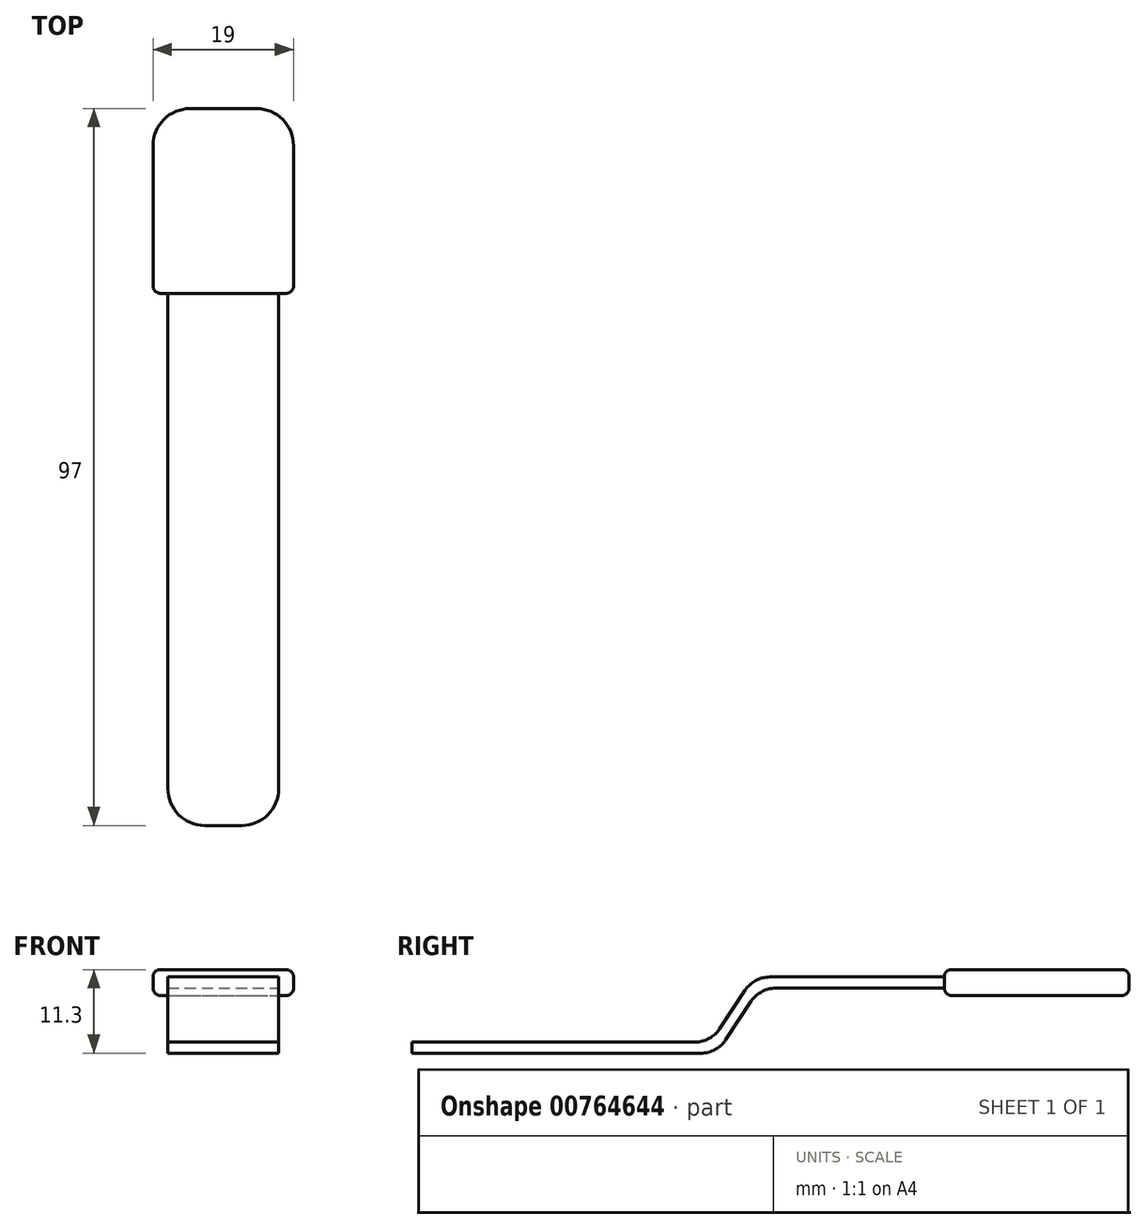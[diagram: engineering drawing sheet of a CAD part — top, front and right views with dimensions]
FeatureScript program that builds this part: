
annotation { "Feature Type Name" : "Feature", "Feature Type Description" : "" }
export const myFeature = defineFeature(function(context is Context, id is Id, definition is map)
    precondition{}
    {
        {
            var Q0;
            Q0=qCreatedBy(makeId("Right.planeOp"),FACE);
            var sketch = newSketch(context, id + "F0", { "sketchPlane" : qUnion([Q0])});
            skLineSegment(sketch, "E0.bottom", {"start": v(-8.38, 4.9) * mm, "end": v(15.22, 4.9) * mm});
            skLineSegment(sketch, "E0.top", {"start": v(-56.78, -5.4) * mm, "end": v(-17.68, -5.4) * mm});
            skLineSegment(sketch, "E0.left", {"start": v(-56.78, -3.9) * mm, "end": v(-56.78, -5.4) * mm});
            skLineSegment(sketch, "E0.right", {"start": v(15.22, 4.9) * mm, "end": v(15.22, 3.4) * mm});
            skPoint(sketch, "E1", {"position": v(-9.78, 4.9) * mm});
            skPoint(sketch, "E2", {"position": v(-14.78, -2.76) * mm});
            skLineSegment(sketch, "E3", {"start": v(15.22, 3.4) * mm, "end": v(-7.57, 3.4) * mm});
            skLineSegment(sketch, "E4", {"start": v(-56.78, -3.9) * mm, "end": v(-18.5, -3.9) * mm});
            skLineSegment(sketch, "E5", {"start": v(-11.72, 3.1) * mm, "end": v(-15.15, -2.1) * mm});
            skLineSegment(sketch, "E6", {"start": v(-10.9, 1.6) * mm, "end": v(-14.35, -3.6) * mm});
            skArc(sketch, "E7.filletArc", {"start": v(-7.57, 3.4) * mm, "mid": v(-9.47, 2.93) * mm, "end": v(-10.9, 1.6) * mm});
            skPoint(sketch, "E8.visualSharp", {"position": v(-10.53, 4.9) * mm});
            skArc(sketch, "E8.filletArc", {"start": v(-8.38, 4.9) * mm, "mid": v(-10.27, 4.43) * mm, "end": v(-11.72, 3.1) * mm});
            skPoint(sketch, "E9.newPointA", {"position": v(-15.53, -2.66) * mm});
            skArc(sketch, "E9.filletArc", {"start": v(-18.5, -3.9) * mm, "mid": v(-16.6, -3.42) * mm, "end": v(-15.15, -2.1) * mm});
            skPoint(sketch, "E10.visualSharp", {"position": v(-15.53, -5.4) * mm});
            skArc(sketch, "E10.filletArc", {"start": v(-17.68, -5.4) * mm, "mid": v(-15.79, -4.92) * mm, "end": v(-14.35, -3.6) * mm});
            skSolve(sketch);
        }
        {
            var Q0;
            Q0=makeQuery(id+"F0.imprint","IMPRINT",FACE,{"disambiguationData":[TD([[makeQuery(id+"F0.imprint","IMPRINT",EDGE,{"derivedFrom":sQuery(id+"F0.wireOp",EDGE,"E0.bottom")}),-1.0]])]});
            extrude(context, id + "F1", {"entities" : qUnion([Q0]), "oppositeDirection" : true, "depth" : 15 * mm, "offsetDistance" : 25 * mm});
        }
        {
            var Q0;
            Q0=makeQuery(id+"F1.opExtrude","CAP_EDGE",EDGE,{"disambiguationData":[OSD([sQuery(id+"F0.wireOp",EDGE,"E0.left")])],"isStart":false});
            var Q1;
            Q1=makeQuery(id+"F1.opExtrude","CAP_EDGE",EDGE,{"disambiguationData":[OSD([sQuery(id+"F0.wireOp",EDGE,"E0.left")])],"isStart":true});
            fillet(context, id + "F2", {"entities" : qUnion([Q0, Q1]), "radius" : 5 * mm, "tangentPropagation" : true, "allowEdgeOverflow" : false});
        }
        {
            var Q0;
            Q0=makeQuery(id+"F1.opExtrude","SWEPT_FACE",FACE,{"disambiguationData":[OSD([sQuery(id+"F0.wireOp",EDGE,"E0.right")])]});
            var sketch = newSketch(context, id + "F3", { "sketchPlane" : qUnion([Q0])});
            skLineSegment(sketch, "E11.bottom", {"start": v(17, 5.9) * mm, "end": v(-2, 5.9) * mm});
            skLineSegment(sketch, "E11.top", {"start": v(17, 2.4) * mm, "end": v(-2, 2.4) * mm});
            skLineSegment(sketch, "E11.left", {"start": v(17, 5.9) * mm, "end": v(17, 2.4) * mm});
            skLineSegment(sketch, "E11.right", {"start": v(-2, 5.9) * mm, "end": v(-2, 2.4) * mm});
            skPoint(sketch, "E11.middle", {"position": v(7.5, 4.16) * mm});
            skPoint(sketch, "E11.middle.positionSnap0", {"position": v(0, 4.16) * mm});
            skPoint(sketch, "E11.middle.positionSnap1", {"position": v(7.5, 4.9) * mm});
            skPoint(sketch, "E11.centerSnap0", {"position": v(0, 4.16) * mm});
            skPoint(sketch, "E11.centerSnap1", {"position": v(7.5, 4.9) * mm});
            skSolve(sketch);
        }
        {
            var Q0;
            Q0 = qSketchRegion(id + "F3", true);
            extrude(context, id + "F4", {"entities" : qUnion([Q0]), "operationType" : NewBodyOperationType.ADD, "depth" : 25 * mm, "offsetDistance" : 25 * mm});
        }
        {
            var Q0;
            Q0=makeQuery(id+"F4.opExtrude","CAP_EDGE",EDGE,{"disambiguationData":[OSD([sQuery(id+"F3.wireOp",EDGE,"E11.right")])],"isStart":false});
            var Q1;
            Q1=makeQuery(id+"F4.opExtrude","CAP_EDGE",EDGE,{"disambiguationData":[OSD([sQuery(id+"F3.wireOp",EDGE,"E11.left")])],"isStart":false});
            fillet(context, id + "F5", {"entities" : qUnion([Q0, Q1]), "radius" : 5 * mm, "tangentPropagation" : true, "allowEdgeOverflow" : false});
        }
        {
            var Q0;
            Q0=makeQuery(id+"F4.opExtrude","SWEPT_FACE",FACE,{"disambiguationData":[OSD([sQuery(id+"F3.wireOp",EDGE,"E11.bottom")])]});
            var Q1;
            Q1=makeQuery(id+"F4.opExtrude","SWEPT_FACE",FACE,{"disambiguationData":[OSD([sQuery(id+"F3.wireOp",EDGE,"E11.top")])]});
            var Q2;
            Q2=makeQuery(id+"F4.opExtrude","CAP_EDGE",EDGE,{"disambiguationData":[OSD([sQuery(id+"F3.wireOp",EDGE,"E11.right")])],"isStart":true});
            var Q3;
            Q3=makeQuery(id+"F4.opExtrude","CAP_EDGE",EDGE,{"disambiguationData":[OSD([sQuery(id+"F3.wireOp",EDGE,"E11.left")])],"isStart":true});
            fillet(context, id + "F6", {"entities" : qUnion([Q0, Q1, Q2, Q3]), "radius" : 1 * mm, "tangentPropagation" : true, "allowEdgeOverflow" : false});
        }
    });
